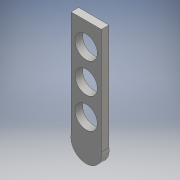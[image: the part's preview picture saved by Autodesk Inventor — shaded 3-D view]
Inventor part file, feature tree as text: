
AUTODESK INVENTOR PART (.ipt)
format: ipt  version: 2016 (Build 200138000, 138)  size: 107,520 bytes
history: native  units: mm
features: extrude x1, sketch x1
ambient origin geometry x8: Origin, YZ Plane, XZ Plane, XY Plane, X Axis, Y Axis, Z Axis, Center Point
bodies: Solid1 (feature_tree)
feature tree (2):
  extrude  "Extrusion1"  Depth=1.5mm
  sketch  "Sketch1"  dims[d0=6.0mm d1=21.0mm d2=4.4mm d3=3.0mm d4=4.5mm d5=4.4mm d6=6.0mm d7=4.4mm d8=6.0mm d10=1.5mm d11=0.0mm]
